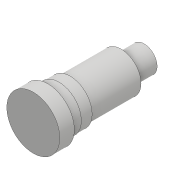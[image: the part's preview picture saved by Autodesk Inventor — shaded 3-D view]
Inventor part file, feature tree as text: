
AUTODESK INVENTOR PART (.ipt)
format: ipt  version: 2018 (Build 220112000, 112)  size: 111,104 bytes
history: native  units: mm
features: revolve x1, sketch x1
ambient origin geometry x8: Origin, YZ Plane, XZ Plane, XY Plane, X Axis, Y Axis, Z Axis, Center Point
bodies: Solid1 (feature_tree)
feature tree (2):
  revolve  "Revolution1"  [1 undecoded]
  sketch  "Sketch1"  dims[d0=1.17mm d1=1.78mm d2=1.97mm d3=2.005mm d4=2.375mm d5=1.3mm d6=7.87mm d7=2.29mm d8=1.0mm d9=1.0mm d10=3.0mm d11=90.0deg]
note: 1 required parameter value undecoded (feature->parameter linkage not recoverable at this tier; creation-order binding heuristic only, values carry confidence <= 0.55)
